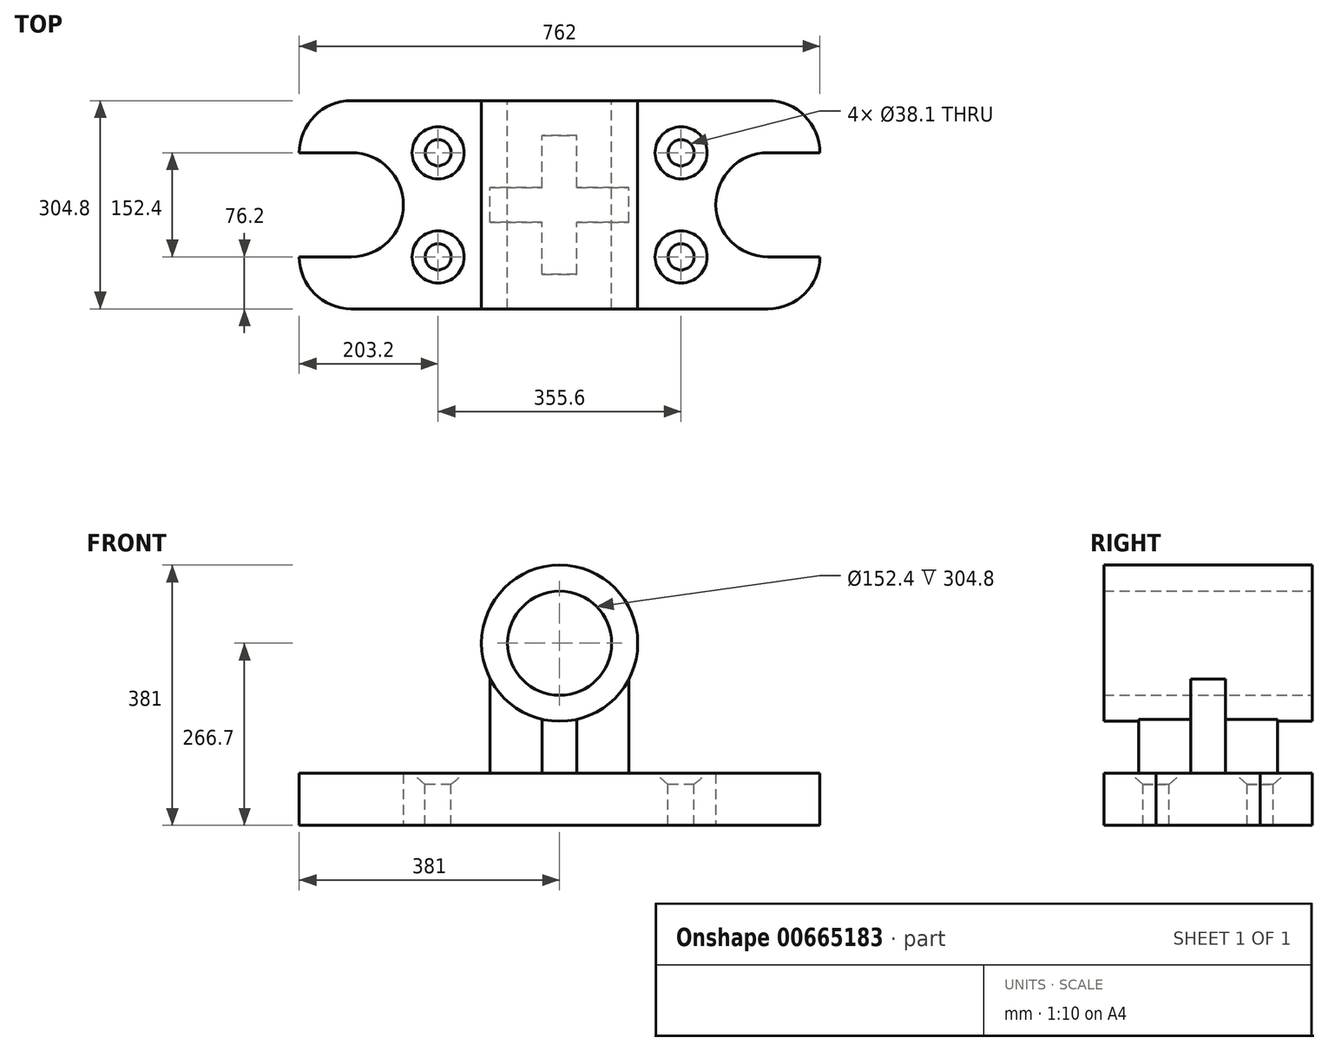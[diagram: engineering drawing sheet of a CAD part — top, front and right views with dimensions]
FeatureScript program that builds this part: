
annotation { "Feature Type Name" : "Feature", "Feature Type Description" : "" }
export const myFeature = defineFeature(function(context is Context, id is Id, definition is map)
    precondition{}
    {
        {
            var Q0;
            Q0=qCreatedBy(makeId("Top.planeOp"),FACE);
            var sketch = newSketch(context, id + "F0", { "sketchPlane" : qUnion([Q0])});
            skLineSegment(sketch, "E0.bottom", {"start": v(101.6, -25.4) * mm, "end": v(25.4, -25.4) * mm});
            skLineSegment(sketch, "E0.top", {"start": v(101.6, 25.4) * mm, "end": v(25.4, 25.4) * mm});
            skLineSegment(sketch, "E0.left", {"start": v(101.6, -25.4) * mm, "end": v(101.6, 25.4) * mm});
            skLineSegment(sketch, "E0.right", {"start": v(-101.6, -25.4) * mm, "end": v(-101.6, 25.4) * mm});
            skPoint(sketch, "E0.middle", {"position": v(0, 0) * mm});
            skLineSegment(sketch, "E1.bottom", {"start": v(25.4, -101.6) * mm, "end": v(-25.4, -101.6) * mm});
            skLineSegment(sketch, "E1.top", {"start": v(25.4, 101.6) * mm, "end": v(-25.4, 101.6) * mm});
            skLineSegment(sketch, "E1.left", {"start": v(25.4, -101.6) * mm, "end": v(25.4, -25.4) * mm});
            skLineSegment(sketch, "E1.right", {"start": v(-25.4, -101.6) * mm, "end": v(-25.4, -25.4) * mm});
            skLineSegment(sketch, "E2.trimOffspring", {"start": v(-25.4, 25.4) * mm, "end": v(-25.4, 101.6) * mm});
            skLineSegment(sketch, "E3.trimOffspring", {"start": v(-25.4, 25.4) * mm, "end": v(-101.6, 25.4) * mm});
            skLineSegment(sketch, "E4.trimOffspring", {"start": v(25.4, 25.4) * mm, "end": v(25.4, 101.6) * mm});
            skLineSegment(sketch, "E5.trimOffspring", {"start": v(-25.4, -25.4) * mm, "end": v(-101.6, -25.4) * mm});
            skArc(sketch, "E6", {"start": v(-304.8, -76.2) * mm, "mid": v(-228.6, 0) * mm, "end": v(-304.8, 76.2) * mm});
            skCircle(sketch, "E7", {"center": v(-177.8, 76.2) * mm, "radius": 38.1 * mm});
            skCircle(sketch, "E8", {"center": v(-177.8, -76.2) * mm, "radius": 38.1 * mm});
            skCircle(sketch, "E9", {"center": v(177.8, 76.2) * mm, "radius": 38.1 * mm});
            skCircle(sketch, "E10", {"center": v(177.8, -76.2) * mm, "radius": 38.1 * mm});
            skLineSegment(sketch, "E11", {"start": v(-304.8, 152.4) * mm, "end": v(304.8, 152.4) * mm});
            skLineSegment(sketch, "E12", {"start": v(304.8, 76.2) * mm, "end": v(381, 76.2) * mm});
            skArc(sketch, "E13", {"start": v(381, 76.2) * mm, "mid": v(358.68, 130.08) * mm, "end": v(304.8, 152.4) * mm});
            skArc(sketch, "E14.MirrorCS", {"start": v(381, -76.2) * mm, "mid": v(358.68, -130.08) * mm, "end": v(304.8, -152.4) * mm});
            skLineSegment(sketch, "E15.MirrorCS", {"start": v(304.8, -76.2) * mm, "end": v(381, -76.2) * mm});
            skArc(sketch, "E16.MirrorCS", {"start": v(-381, 76.2) * mm, "mid": v(-358.68, 130.08) * mm, "end": v(-304.8, 152.4) * mm});
            skLineSegment(sketch, "E17.MirrorCS", {"start": v(-304.8, 76.2) * mm, "end": v(-381, 76.2) * mm});
            skLineSegment(sketch, "E18.MirrorCS", {"start": v(-304.8, -76.2) * mm, "end": v(-381, -76.2) * mm});
            skArc(sketch, "E19.MirrorCS", {"start": v(-381, -76.2) * mm, "mid": v(-358.68, -130.08) * mm, "end": v(-304.8, -152.4) * mm});
            skLineSegment(sketch, "E20", {"start": v(-304.8, -152.4) * mm, "end": v(304.8, -152.4) * mm});
            skArc(sketch, "E21.MirrorCS", {"start": v(304.8, -76.2) * mm, "mid": v(228.6, 0) * mm, "end": v(304.8, 76.2) * mm});
            skSolve(sketch);
        }
        {
            var Q0;
            Q0=makeQuery(id+"F0.imprint","IMPRINT",FACE,{"disambiguationData":[TD([[makeQuery(id+"F0.imprint","IMPRINT",EDGE,{"derivedFrom":sQuery(id+"F0.wireOp",EDGE,"E0.bottom")}),1.0]])]});
            var Q1;
            Q1=makeQuery(id+"F0.imprint","IMPRINT",FACE,{"disambiguationData":[TD([[makeQuery(id+"F0.imprint","IMPRINT",EDGE,{"derivedFrom":sQuery(id+"F0.wireOp",EDGE,"E7")}),1.0]])]});
            var Q2;
            Q2=makeQuery(id+"F0.imprint","IMPRINT",FACE,{"disambiguationData":[TD([[makeQuery(id+"F0.imprint","IMPRINT",EDGE,{"derivedFrom":sQuery(id+"F0.wireOp",EDGE,"E8")}),1.0]])]});
            var Q3;
            Q3=makeQuery(id+"F0.imprint","IMPRINT",FACE,{"disambiguationData":[TD([[makeQuery(id+"F0.imprint","IMPRINT",EDGE,{"derivedFrom":sQuery(id+"F0.wireOp",EDGE,"E10")}),1.0]])]});
            var Q4;
            Q4=makeQuery(id+"F0.imprint","IMPRINT",FACE,{"disambiguationData":[TD([[makeQuery(id+"F0.imprint","IMPRINT",EDGE,{"derivedFrom":sQuery(id+"F0.wireOp",EDGE,"E9")}),1.0]])]});
            extrude(context, id + "F1", {"entities" : qUnion([Q0, Q1, Q2, Q3, Q4]), "depth" : 76.2 * mm, "offsetDistance" : 25.4 * mm});
        }
        {
            var Q0;
            Q0=makeQuery(id+"F0.imprint","IMPRINT",FACE,{"disambiguationData":[TD([[makeQuery(id+"F0.imprint","IMPRINT",EDGE,{"derivedFrom":sQuery(id+"F0.wireOp",EDGE,"E0.bottom")}),-1.0]])]});
            extrude(context, id + "F2", {"entities" : qUnion([Q0]), "operationType" : NewBodyOperationType.ADD, "depth" : 266.7 * mm, "offsetDistance" : 25.4 * mm});
        }
        {
            var Q0;
            Q0=makeQuery(id+"F1.opExtrude","CAP_FACE",FACE,{"disambiguationData":[OSD([sQuery(id+"F0.wireOp",EDGE,"E0.bottom"),sQuery(id+"F0.wireOp",EDGE,"E0.top"),sQuery(id+"F0.wireOp",EDGE,"E0.left"),sQuery(id+"F0.wireOp",EDGE,"E0.right"),sQuery(id+"F0.wireOp",EDGE,"E1.bottom"),sQuery(id+"F0.wireOp",EDGE,"E1.top"),sQuery(id+"F0.wireOp",EDGE,"E1.left"),sQuery(id+"F0.wireOp",EDGE,"E1.right"),sQuery(id+"F0.wireOp",EDGE,"E2.trimOffspring"),sQuery(id+"F0.wireOp",EDGE,"E3.trimOffspring"),sQuery(id+"F0.wireOp",EDGE,"E4.trimOffspring"),sQuery(id+"F0.wireOp",EDGE,"E5.trimOffspring"),sQuery(id+"F0.wireOp",EDGE,"E6"),sQuery(id+"F0.wireOp",EDGE,"E11"),sQuery(id+"F0.wireOp",EDGE,"E12"),sQuery(id+"F0.wireOp",EDGE,"E13"),sQuery(id+"F0.wireOp",EDGE,"E14.MirrorCS"),sQuery(id+"F0.wireOp",EDGE,"E15.MirrorCS"),sQuery(id+"F0.wireOp",EDGE,"E16.MirrorCS"),sQuery(id+"F0.wireOp",EDGE,"E17.MirrorCS"),sQuery(id+"F0.wireOp",EDGE,"E18.MirrorCS"),sQuery(id+"F0.wireOp",EDGE,"E19.MirrorCS"),sQuery(id+"F0.wireOp",EDGE,"E20"),sQuery(id+"F0.wireOp",EDGE,"E21.MirrorCS")])],"isStart":false});
            var sketch = newSketch(context, id + "F3", { "sketchPlane" : qUnion([Q0])});
            skPoint(sketch, "E22.0", {"position": v(177.8, -76.2) * mm});
            skPoint(sketch, "E23.0", {"position": v(177.8, 76.2) * mm});
            skPoint(sketch, "E24.0", {"position": v(-177.8, 76.2) * mm});
            skPoint(sketch, "E25.0", {"position": v(-177.8, -76.2) * mm});
            skSolve(sketch);
        }
        {
            var Q0;
            Q0=sQuery(id+"F3.wireOp",VERTEX,"E25.0");
            var Q1;
            Q1=sQuery(id+"F3.wireOp",VERTEX,"E24.0");
            var Q2;
            Q2=sQuery(id+"F3.wireOp",VERTEX,"E23.0");
            var Q3;
            Q3=sQuery(id+"F3.wireOp",VERTEX,"E22.0");
            var Q4;
            Q4=makeQuery(id+"F1.opExtrude","SWEPT_BODY",BODY,{"disambiguationData":[OSD([sQuery(id+"F0.wireOp",EDGE,"E0.bottom"),sQuery(id+"F0.wireOp",EDGE,"E0.top"),sQuery(id+"F0.wireOp",EDGE,"E0.left"),sQuery(id+"F0.wireOp",EDGE,"E0.right"),sQuery(id+"F0.wireOp",EDGE,"E1.bottom"),sQuery(id+"F0.wireOp",EDGE,"E1.top"),sQuery(id+"F0.wireOp",EDGE,"E1.left"),sQuery(id+"F0.wireOp",EDGE,"E1.right"),sQuery(id+"F0.wireOp",EDGE,"E2.trimOffspring"),sQuery(id+"F0.wireOp",EDGE,"E3.trimOffspring"),sQuery(id+"F0.wireOp",EDGE,"E4.trimOffspring"),sQuery(id+"F0.wireOp",EDGE,"E5.trimOffspring"),sQuery(id+"F0.wireOp",EDGE,"E6"),sQuery(id+"F0.wireOp",EDGE,"E11"),sQuery(id+"F0.wireOp",EDGE,"E12"),sQuery(id+"F0.wireOp",EDGE,"E13"),sQuery(id+"F0.wireOp",EDGE,"E14.MirrorCS"),sQuery(id+"F0.wireOp",EDGE,"E15.MirrorCS"),sQuery(id+"F0.wireOp",EDGE,"E16.MirrorCS"),sQuery(id+"F0.wireOp",EDGE,"E17.MirrorCS"),sQuery(id+"F0.wireOp",EDGE,"E18.MirrorCS"),sQuery(id+"F0.wireOp",EDGE,"E19.MirrorCS"),sQuery(id+"F0.wireOp",EDGE,"E20"),sQuery(id+"F0.wireOp",EDGE,"E21.MirrorCS")])]});
            hole(context, id + "F4", {"style" : HoleStyle.C_SINK, "endStyle" : HoleEndStyle.THROUGH, "holeDiameter" : 38.1 * mm, "cSinkDiameter" : 76.2 * mm, "cSinkAngle" : 100 * degree, "majorDiameter" : 6.35 * mm, "isTappedThrough" : true, "tappedDepth" : 12.7 * mm, "tapClearance" : 3, "locations" : qUnion([Q0, Q1, Q2, Q3]), "scope" : qUnion([Q4])});
        }
        {
            var Q0;
            Q0=qCreatedBy(makeId("Front.planeOp"),FACE);
            var sketch = newSketch(context, id + "F5", { "sketchPlane" : qUnion([Q0])});
            skCircle(sketch, "E26", {"center": v(0, 266.7) * mm, "radius": 114.3 * mm});
            skCircle(sketch, "E27", {"center": v(0, 266.7) * mm, "radius": 76.2 * mm});
            skSolve(sketch);
        }
        {
            var Q0;
            Q0=makeQuery(id+"F5.imprint","IMPRINT",FACE,{"disambiguationData":[TD([[makeQuery(id+"F5.imprint","IMPRINT",EDGE,{"derivedFrom":sQuery(id+"F5.wireOp",EDGE,"E26")}),1.0]])]});
            extrude(context, id + "F6", {"entities" : qUnion([Q0]), "operationType" : NewBodyOperationType.ADD, "endBound" : BoundingType.SYMMETRIC, "depth" : 304.8 * mm, "offsetDistance" : 25.4 * mm});
        }
        {
            var Q0;
            Q0=makeQuery(id+"F5.imprint","IMPRINT",FACE,{"disambiguationData":[TD([[makeQuery(id+"F5.imprint","IMPRINT",EDGE,{"derivedFrom":sQuery(id+"F5.wireOp",EDGE,"E27")}),1.0]])]});
            extrude(context, id + "F7", {"entities" : qUnion([Q0]), "operationType" : NewBodyOperationType.REMOVE, "endBound" : BoundingType.SYMMETRIC, "oppositeDirection" : true, "depth" : 304.8 * mm, "offsetDistance" : 25.4 * mm});
        }
    });
